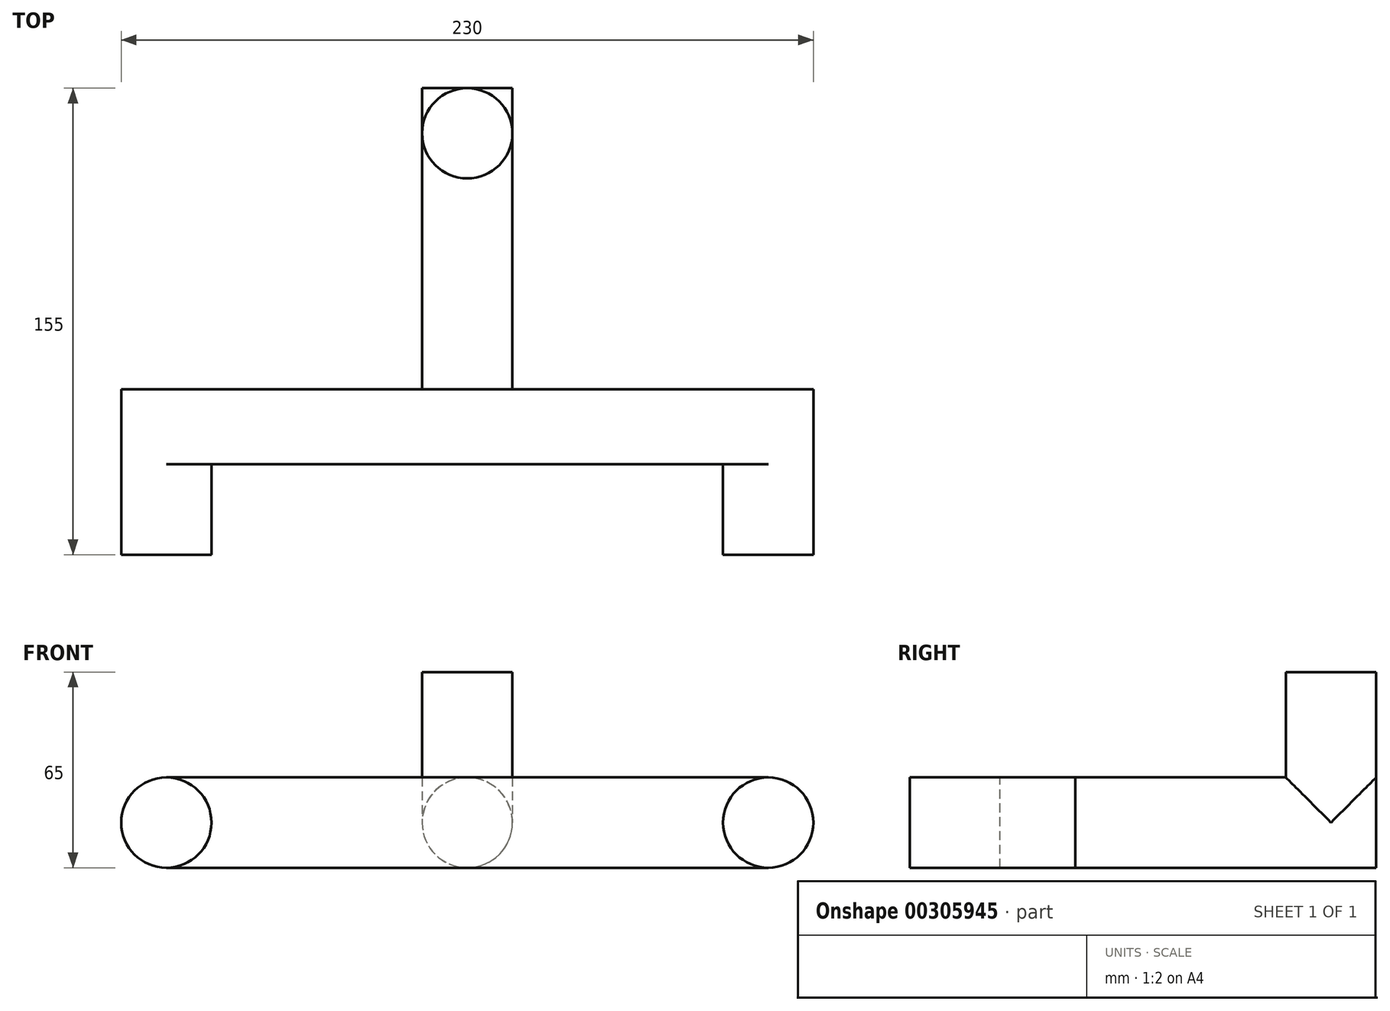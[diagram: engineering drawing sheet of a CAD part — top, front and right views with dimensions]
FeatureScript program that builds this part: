
annotation { "Feature Type Name" : "Feature", "Feature Type Description" : "" }
export const myFeature = defineFeature(function(context is Context, id is Id, definition is map)
    precondition{}
    {
        {
            var Q0;
            Q0=qCreatedBy(makeId("Front.planeOp"),FACE);
            var sketch = newSketch(context, id + "F0", { "sketchPlane" : qUnion([Q0])});
            skCircle(sketch, "E0", {"center": v(100, 0) * mm, "radius": 15 * mm});
            skCircle(sketch, "E1", {"center": v(-100, 0) * mm, "radius": 15 * mm});
            skLineSegment(sketch, "E2", {"start": v(-100, 0) * mm, "end": v(-100, 15) * mm});
            skLineSegment(sketch, "E3", {"start": v(100, 0) * mm, "end": v(100, -15) * mm});
            skLineSegment(sketch, "E4.bottom", {"start": v(-100, 15) * mm, "end": v(100, 15) * mm});
            skLineSegment(sketch, "E4.top", {"start": v(-100, -15) * mm, "end": v(100, -15) * mm});
            skLineSegment(sketch, "E4.left", {"start": v(-100, 15) * mm, "end": v(-100, -15) * mm});
            skLineSegment(sketch, "E4.right", {"start": v(100, 15) * mm, "end": v(100, -15) * mm});
            skSolve(sketch);
        }
        {
            var Q0;
            {var subQ0=sQuery(id+"F0.wireOp",EDGE,"E4.left");var subQ4=makeQuery(id+"F0.imprint","IMPRINT",VERTEX,{"derivedFrom":subQ0});Q0=makeQuery(id+"F0.imprint","IMPRINT",FACE,{"disambiguationData":[TD([[makeQuery(id+"F0.imprint","IMPRINT",EDGE,{"disambiguationData":[TD([[subQ4,1.0]])],"derivedFrom":subQ0}),-1.0]])]});}
            var Q1;
            {var subQ0=sQuery(id+"F0.wireOp",EDGE,"E4.left");var subQ4=makeQuery(id+"F0.imprint","IMPRINT",VERTEX,{"derivedFrom":subQ0});Q1=makeQuery(id+"F0.imprint","IMPRINT",FACE,{"disambiguationData":[TD([[makeQuery(id+"F0.imprint","IMPRINT",EDGE,{"disambiguationData":[TD([[subQ4,1.0]])],"derivedFrom":subQ0}),1.0]])]});}
            var Q2;
            {var subQ1=sQuery(id+"F0.wireOp",EDGE,"E4.bottom");Q2=makeQuery(id+"F0.imprint","IMPRINT",FACE,{"disambiguationData":[TD([[makeQuery(id+"F0.imprint","IMPRINT",EDGE,{"derivedFrom":subQ1}),-1.0]])]});}
            var Q3;
            {var subQ0=sQuery(id+"F0.wireOp",EDGE,"E4.right");var subQ4=makeQuery(id+"F0.imprint","IMPRINT",VERTEX,{"derivedFrom":subQ0});Q3=makeQuery(id+"F0.imprint","IMPRINT",FACE,{"disambiguationData":[TD([[makeQuery(id+"F0.imprint","IMPRINT",EDGE,{"disambiguationData":[TD([[subQ4,1.0]])],"derivedFrom":subQ0}),-1.0]])]});}
            var Q4;
            {var subQ0=sQuery(id+"F0.wireOp",EDGE,"E4.right");var subQ4=makeQuery(id+"F0.imprint","IMPRINT",VERTEX,{"derivedFrom":subQ0});Q4=makeQuery(id+"F0.imprint","IMPRINT",FACE,{"disambiguationData":[TD([[makeQuery(id+"F0.imprint","IMPRINT",EDGE,{"disambiguationData":[TD([[subQ4,1.0]])],"derivedFrom":subQ0}),1.0]])]});}
            extrude(context, id + "F1", {"entities" : qUnion([Q0, Q1, Q2, Q3, Q4]), "depth" : 25 * mm});
        }
        {
            var Q0;
            Q0=makeQuery(id+"F1.opExtrude","CAP_FACE",FACE,{"disambiguationData":[OSD([sQuery(id+"F0.wireOp",EDGE,"E0"),sQuery(id+"F0.wireOp",EDGE,"E1"),sQuery(id+"F0.wireOp",EDGE,"E4.bottom"),sQuery(id+"F0.wireOp",EDGE,"E4.top")])],"isStart":false});
            var sketch = newSketch(context, id + "F2", { "sketchPlane" : qUnion([Q0])});
            skCircle(sketch, "E5", {"center": v(100, 0) * mm, "radius": 15 * mm});
            skPoint(sketch, "E5.first.point", {"position": v(100, 15) * mm});
            skPoint(sketch, "E5.second.point", {"position": v(100, -15) * mm});
            skPoint(sketch, "E5.third.point", {"position": v(115, 0) * mm});
            skCircle(sketch, "E6", {"center": v(-100, 0) * mm, "radius": 15 * mm});
            skPoint(sketch, "E6.first.point", {"position": v(-100, 15) * mm});
            skPoint(sketch, "E6.second.point", {"position": v(-100, -15) * mm});
            skPoint(sketch, "E6.third.point", {"position": v(-115, 0) * mm});
            skSolve(sketch);
        }
        {
            var Q0;
            {var subQ0=sQuery(id+"F2.wireOp",EDGE,"E6");var subQ1=makeQuery(id+"F2.imprint","INTERSECT",VERTEX,{"derivedFrom":[makeQuery(id+"F1.opExtrude","CAP_EDGE",EDGE,{"disambiguationData":[OSD([sQuery(id+"F0.wireOp",EDGE,"E4.bottom")])],"isStart":false}),subQ0]});Q0=makeQuery(id+"F2.imprint","IMPRINT",FACE,{"disambiguationData":[TD([[makeQuery(id+"F2.imprint","IMPRINT",EDGE,{"disambiguationData":[TD([[subQ1,-1.0]])],"derivedFrom":subQ0}),1.0]])]});}
            var Q1;
            {var subQ0=sQuery(id+"F2.wireOp",EDGE,"E5");var subQ1=makeQuery(id+"F2.imprint","INTERSECT",VERTEX,{"derivedFrom":[makeQuery(id+"F1.opExtrude","CAP_EDGE",EDGE,{"disambiguationData":[OSD([sQuery(id+"F0.wireOp",EDGE,"E4.bottom")])],"isStart":false}),subQ0]});Q1=makeQuery(id+"F2.imprint","IMPRINT",FACE,{"disambiguationData":[TD([[makeQuery(id+"F2.imprint","IMPRINT",EDGE,{"disambiguationData":[TD([[subQ1,-1.0]])],"derivedFrom":subQ0}),1.0]])]});}
            extrude(context, id + "F3", {"entities" : qUnion([Q0, Q1]), "operationType" : NewBodyOperationType.ADD, "depth" : 30 * mm});
        }
        {
            var Q0;
            Q0=makeQuery(id+"F1.opExtrude","CAP_FACE",FACE,{"disambiguationData":[OSD([sQuery(id+"F0.wireOp",EDGE,"E0"),sQuery(id+"F0.wireOp",EDGE,"E1"),sQuery(id+"F0.wireOp",EDGE,"E4.bottom"),sQuery(id+"F0.wireOp",EDGE,"E4.top")])],"isStart":true});
            var sketch = newSketch(context, id + "F4", { "sketchPlane" : qUnion([Q0])});
            skCircle(sketch, "E7", {"center": v(0, 0) * mm, "radius": 15 * mm});
            skSolve(sketch);
        }
        {
            var Q0;
            {var subQ0=sQuery(id+"F4.wireOp",EDGE,"E7");var subQ1=makeQuery(id+"F4.imprint","INTERSECT",VERTEX,{"derivedFrom":[makeQuery(id+"F1.opExtrude","CAP_EDGE",EDGE,{"disambiguationData":[OSD([sQuery(id+"F0.wireOp",EDGE,"E4.bottom")])],"isStart":true}),subQ0]});Q0=makeQuery(id+"F4.imprint","IMPRINT",FACE,{"disambiguationData":[TD([[makeQuery(id+"F4.imprint","IMPRINT",EDGE,{"disambiguationData":[TD([[subQ1,-1.0]])],"derivedFrom":subQ0}),1.0]])]});}
            extrude(context, id + "F5", {"entities" : qUnion([Q0]), "operationType" : NewBodyOperationType.ADD, "depth" : 100 * mm});
        }
        {
            var Q0;
            Q0=qCreatedBy(makeId("Top.planeOp"),FACE);
            var sketch = newSketch(context, id + "F6", { "sketchPlane" : qUnion([Q0])});
            skLineSegment(sketch, "E8", {"start": v(0, 0) * mm, "end": v(0, 100) * mm});
            skLineSegment(sketch, "E9", {"start": v(0, 100) * mm, "end": v(0, 85) * mm});
            skCircle(sketch, "E10", {"center": v(0, 85) * mm, "radius": 15 * mm});
            skSolve(sketch);
        }
        {
            var Q0;
            Q0 = qSketchRegion(id + "F6", true);
            extrude(context, id + "F7", {"entities" : qUnion([Q0]), "operationType" : NewBodyOperationType.ADD, "depth" : 50 * mm});
        }
    });
